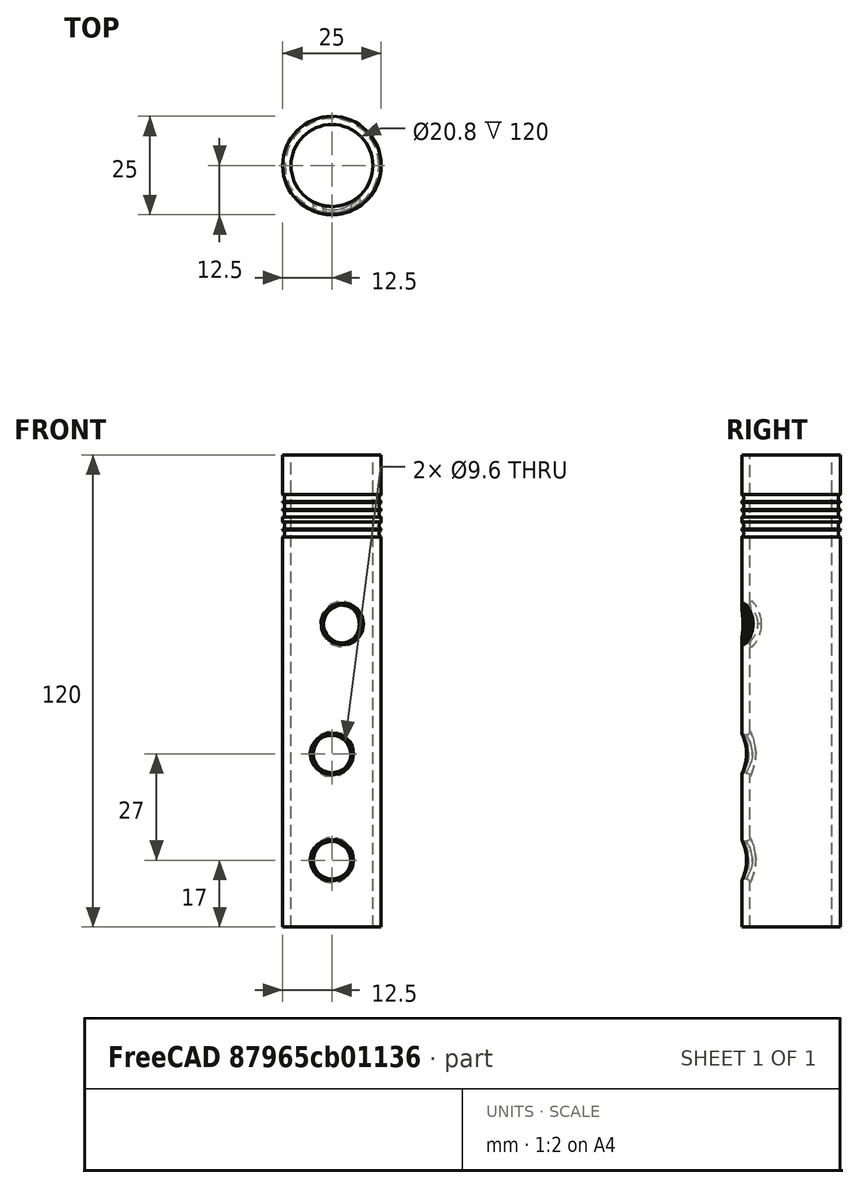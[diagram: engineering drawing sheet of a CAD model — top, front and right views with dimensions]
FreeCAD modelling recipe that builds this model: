
FCSTD DOCUMENT
Label: Part5
License: CC-BY 3.0
LicenseURL: http://creativecommons.org/licenses/by/3.0/
objects: Part::Cut×9, Part::Cylinder×5, Part::Torus×5, PartDesign::Fillet×2
note: 21 computed .brp shape members not serialized (recipe doc carries the construction recipe); baked Part::Feature solids carry a one-line shape summary decoded from their .brp

FEATURE [Part::Cylinder] Cylinder
  Angle = 360
  Height = 120
  Radius = 12.5
FEATURE [Part::Cylinder] Cylinder001
  Angle = 360
  Height = 120
  Radius = 10.4
FEATURE [Part::Torus] Torus
  Angle1 = -180
  Angle2 = 180
  Angle3 = 360
  Placement = pos=(0,0,102) rot=(0,0,1;0rad)
  Radius1 = 13
  Radius2 = 1
FEATURE [Part::Torus] Torus001
  Angle1 = -180
  Angle2 = 180
  Angle3 = 360
  Placement = pos=(0,0,100) rot=(0,0,1;0rad)
  Radius1 = 13
  Radius2 = 1
FEATURE [Part::Cylinder] Cylinder006  label="Segiah"
  Angle = 360
  Height = 10
  Placement = pos=(0,-8,17) rot=(1,0,0;1.5708rad)
  Radius = 4.8
FEATURE [Part::Cylinder] Cylinder006001001  label="Dugah"
  Angle = 360
  Height = 10
  Placement = pos=(2,-8,77) rot=(0.990855,0.095409,0.095409;1.57998rad)
  Radius = 4.8
FEATURE [Part::Torus] Torus001001
  Angle1 = -180
  Angle2 = 180
  Angle3 = 360
  Placement = pos=(0,0,109) rot=(0,0,1;0rad)
  Radius1 = 13
  Radius2 = 1
FEATURE [Part::Torus] Torus001002
  Angle1 = -180
  Angle2 = 180
  Angle3 = 360
  Placement = pos=(0,0,107) rot=(0,0,1;0rad)
  Radius1 = 13
  Radius2 = 1
FEATURE [Part::Torus] Torus001002001
  Angle1 = -180
  Angle2 = 180
  Angle3 = 360
  Placement = pos=(0,0,105) rot=(0,0,1;0rad)
  Radius1 = 13
  Radius2 = 1
FEATURE [Part::Cut] Cut
  Base = -> Cylinder
  Tool = -> Cylinder001
FEATURE [Part::Cylinder] Cylinder006001  label="Kurdi"
  Angle = 360
  Height = 10
  Placement = pos=(0,-8,44) rot=(1,0,0;1.5708rad)
  Radius = 4.8
FEATURE [Part::Cut] Cut001
  Base = -> Cut
  Tool = -> Cylinder006001
FEATURE [Part::Cut] Cut002
  Base = -> Cut001
  Tool = -> Cylinder006
FEATURE [Part::Cut] Cut003
  Base = -> Cut002
  Tool = -> Cylinder006001001
FEATURE [Part::Cut] Cut004
  Base = -> Cut003
  Tool = -> Torus001002
FEATURE [Part::Cut] Cut005
  Base = -> Cut004
  Tool = -> Torus001002001
FEATURE [Part::Cut] Cut006
  Base = -> Cut005
  Tool = -> Torus
FEATURE [Part::Cut] Cut007
  Base = -> Cut006
  Tool = -> Torus001
FEATURE [Part::Cut] Cut008
  Base = -> Cut007
  Tool = -> Torus001001
FEATURE [PartDesign::Fillet] Fillet
  Base = -> Cut008 [Edge5,Edge4,Edge6]
  Radius = 0.5
FEATURE [PartDesign::Fillet] Fillet001
  Base = -> Fillet [Edge23,Edge22,Edge17]
  Radius = 1
